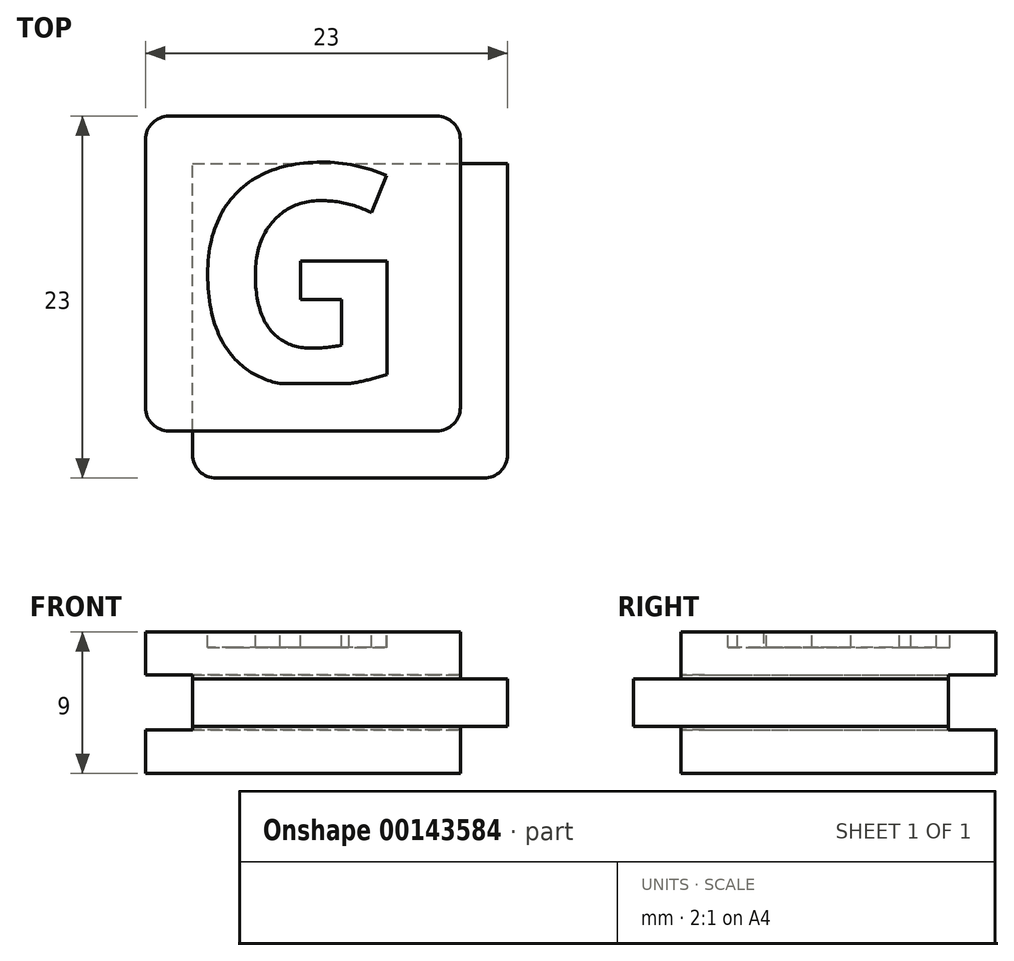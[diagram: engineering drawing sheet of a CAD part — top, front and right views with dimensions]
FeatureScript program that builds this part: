
annotation { "Feature Type Name" : "Feature", "Feature Type Description" : "" }
export const myFeature = defineFeature(function(context is Context, id is Id, definition is map)
    precondition{}
    {
        {
            var Q0;
            Q0=qCreatedBy(makeId("Front.planeOp"),FACE);
            var sketch = newSketch(context, id + "F0", { "sketchPlane" : qUnion([Q0])});
            skLineSegment(sketch, "E0.bottom", {"start": v(10, 4.5) * mm, "end": v(-10, 4.5) * mm});
            skLineSegment(sketch, "E0.top", {"start": v(10, -4.5) * mm, "end": v(-10, -4.5) * mm});
            skLineSegment(sketch, "E0.left", {"start": v(10, 4.5) * mm, "end": v(10, -4.5) * mm});
            skLineSegment(sketch, "E0.right", {"start": v(-10, 4.5) * mm, "end": v(-10, -4.5) * mm});
            skPoint(sketch, "E0.middle", {"position": v(0, 0) * mm});
            skLineSegment(sketch, "E1.bottom", {"start": v(13, 1.5) * mm, "end": v(7, 1.5) * mm});
            skLineSegment(sketch, "E1.top", {"start": v(13, -1.5) * mm, "end": v(7, -1.5) * mm});
            skLineSegment(sketch, "E1.left", {"start": v(13, 1.5) * mm, "end": v(13, -1.5) * mm});
            skLineSegment(sketch, "E1.right", {"start": v(7, 1.5) * mm, "end": v(7, -1.5) * mm});
            skPoint(sketch, "E1.middle", {"position": v(10, 0) * mm});
            skLineSegment(sketch, "E2.bottom", {"start": v(7, 1.5) * mm, "end": v(-7, 1.5) * mm});
            skLineSegment(sketch, "E2.top", {"start": v(7, -1.5) * mm, "end": v(-7, -1.5) * mm});
            skLineSegment(sketch, "E2.right", {"start": v(-7, 1.5) * mm, "end": v(-7, -1.5) * mm});
            skLineSegment(sketch, "E3.bottom", {"start": v(-7, -1.5) * mm, "end": v(-10, -1.5) * mm});
            skLineSegment(sketch, "E3.top", {"start": v(-7, 1.5) * mm, "end": v(-10, 1.5) * mm});
            skLineSegment(sketch, "E3.left", {"start": v(-7, -1.5) * mm, "end": v(-7, 1.5) * mm});
            skLineSegment(sketch, "E3.right", {"start": v(-10, -1.5) * mm, "end": v(-10, 1.5) * mm});
            skSolve(sketch);
        }
        {
            var Q0;
            {var subQ5=sQuery(id+"F0.wireOp",EDGE,"E0.bottom");Q0=makeQuery(id+"F0.imprint","IMPRINT",FACE,{"disambiguationData":[TD([[makeQuery(id+"F0.imprint","IMPRINT",EDGE,{"derivedFrom":subQ5}),1.0]])]});}
            var Q1;
            Q1=makeQuery(id+"F0.imprint","IMPRINT",FACE,{"disambiguationData":[TD([[makeQuery(id+"F0.imprint","IMPRINT",EDGE,{"derivedFrom":sQuery(id+"F0.wireOp",EDGE,"E2.bottom")}),1.0]])]});
            var Q2;
            {var subQ5=sQuery(id+"F0.wireOp",EDGE,"E1.left");Q2=makeQuery(id+"F0.imprint","IMPRINT",FACE,{"disambiguationData":[TD([[makeQuery(id+"F0.imprint","IMPRINT",EDGE,{"derivedFrom":subQ5}),-1.0]])]});}
            var Q3;
            {var subQ5=sQuery(id+"F0.wireOp",EDGE,"E1.right");Q3=makeQuery(id+"F0.imprint","IMPRINT",FACE,{"disambiguationData":[TD([[makeQuery(id+"F0.imprint","IMPRINT",EDGE,{"derivedFrom":subQ5}),1.0]])]});}
            var Q4;
            Q4=makeQuery(id+"F0.imprint","IMPRINT",FACE,{"disambiguationData":[TD([[makeQuery(id+"F0.imprint","IMPRINT",EDGE,{"derivedFrom":sQuery(id+"F0.wireOp",EDGE,"E3.bottom")}),-1.0]])]});
            var Q5;
            {var subQ5=sQuery(id+"F0.wireOp",EDGE,"E0.top");Q5=makeQuery(id+"F0.imprint","IMPRINT",FACE,{"disambiguationData":[TD([[makeQuery(id+"F0.imprint","IMPRINT",EDGE,{"derivedFrom":subQ5}),-1.0]])]});}
            extrude(context, id + "F1", {"entities" : qUnion([Q0, Q1, Q2, Q3, Q4, Q5]), "oppositeDirection" : true, "depth" : 20 * mm});
        }
        {
            var Q0;
            Q0=makeQuery(id+"F0.imprint","IMPRINT",FACE,{"disambiguationData":[TD([[makeQuery(id+"F0.imprint","IMPRINT",EDGE,{"derivedFrom":sQuery(id+"F0.wireOp",EDGE,"E3.bottom")}),-1.0]])]});
            var Q1;
            Q1=makeQuery(id+"F0.imprint","IMPRINT",FACE,{"disambiguationData":[TD([[makeQuery(id+"F0.imprint","IMPRINT",EDGE,{"derivedFrom":sQuery(id+"F0.wireOp",EDGE,"E2.bottom")}),1.0]])]});
            var Q2;
            {var subQ5=sQuery(id+"F0.wireOp",EDGE,"E1.right");Q2=makeQuery(id+"F0.imprint","IMPRINT",FACE,{"disambiguationData":[TD([[makeQuery(id+"F0.imprint","IMPRINT",EDGE,{"derivedFrom":subQ5}),1.0]])]});}
            var Q3;
            {var subQ5=sQuery(id+"F0.wireOp",EDGE,"E1.left");Q3=makeQuery(id+"F0.imprint","IMPRINT",FACE,{"disambiguationData":[TD([[makeQuery(id+"F0.imprint","IMPRINT",EDGE,{"derivedFrom":subQ5}),-1.0]])]});}
            extrude(context, id + "F2", {"entities" : qUnion([Q0, Q1, Q2, Q3]), "operationType" : NewBodyOperationType.ADD, "depth" : 3 * mm});
        }
        {
            var Q0;
            {var subQ0=sQuery(id+"F0.wireOp",EDGE,"E1.left");Q0=makeQuery(id+"F2.boolean.opBoolean","MERGE",FACE,{"derivedFrom":[makeQuery(id+"F1.opExtrude","SWEPT_FACE",FACE,{"disambiguationData":[OSD([subQ0])]}),makeQuery(id+"F2.opExtrude","SWEPT_FACE",FACE,{"disambiguationData":[OSD([subQ0])]})]});}
            var sketch = newSketch(context, id + "F3", { "sketchPlane" : qUnion([Q0])});
            skLineSegment(sketch, "E4.bottom", {"start": v(23, 1.75) * mm, "end": v(17, 1.75) * mm});
            skLineSegment(sketch, "E4.top", {"start": v(23, -1.75) * mm, "end": v(17, -1.75) * mm});
            skLineSegment(sketch, "E4.left", {"start": v(23, 1.75) * mm, "end": v(23, -1.75) * mm});
            skLineSegment(sketch, "E4.right", {"start": v(17, 1.75) * mm, "end": v(17, -1.75) * mm});
            skPoint(sketch, "E4.middle", {"position": v(20, 0) * mm});
            skSolve(sketch);
        }
        {
            var Q0;
            {var subQ1=sQuery(id+"F3.wireOp",EDGE,"E4.bottom");Q0=makeQuery(id+"F3.imprint","IMPRINT",FACE,{"disambiguationData":[TD([[makeQuery(id+"F3.imprint","IMPRINT",EDGE,{"derivedFrom":subQ1}),1.0]])]});}
            var Q1;
            {var subQ1=sQuery(id+"F0.wireOp",EDGE,"E1.left");var subQ8=makeQuery(id+"F1.opExtrude","CAP_EDGE",EDGE,{"disambiguationData":[OSD([subQ1])],"isStart":false});Q1=makeQuery(id+"F3.imprint","IMPRINT",FACE,{"disambiguationData":[TD([[makeQuery(id+"F3.imprint","IMPRINT",EDGE,{"derivedFrom":subQ8}),-1.0]])]});}
            extrude(context, id + "F4", {"entities" : qUnion([Q0, Q1]), "operationType" : NewBodyOperationType.REMOVE, "oppositeDirection" : true, "depth" : 100 * mm});
        }
        {
            var Q0;
            Q0=makeQuery(id+"F4.boolean.opBoolean","COPY",FACE,{"derivedFrom":makeQuery(id+"F4.opExtrude","SWEPT_FACE",FACE,{"disambiguationData":[OSD([sQuery(id+"F3.wireOp",EDGE,"E4.right")])]})});
            var sketch = newSketch(context, id + "F5", { "sketchPlane" : qUnion([Q0])});
            skLineSegment(sketch, "E5.bottom", {"start": v(13, 1.75) * mm, "end": v(7, 1.75) * mm});
            skLineSegment(sketch, "E5.top", {"start": v(13, -1.75) * mm, "end": v(7, -1.75) * mm});
            skLineSegment(sketch, "E5.left", {"start": v(13, 1.75) * mm, "end": v(13, -1.75) * mm});
            skLineSegment(sketch, "E5.right", {"start": v(7, 1.75) * mm, "end": v(7, -1.75) * mm});
            skPoint(sketch, "E5.middle", {"position": v(10, 0) * mm});
            skSolve(sketch);
        }
        {
            var Q0;
            {var subQ3=sQuery(id+"F5.wireOp",EDGE,"E5.left");Q0=makeQuery(id+"F5.imprint","IMPRINT",FACE,{"disambiguationData":[TD([[makeQuery(id+"F5.imprint","IMPRINT",EDGE,{"derivedFrom":subQ3}),-1.0]])]});}
            var Q1;
            {var subQ4=sQuery(id+"F5.wireOp",EDGE,"E5.right");Q1=makeQuery(id+"F5.imprint","IMPRINT",FACE,{"disambiguationData":[TD([[makeQuery(id+"F5.imprint","IMPRINT",EDGE,{"derivedFrom":subQ4}),1.0]])]});}
            extrude(context, id + "F6", {"entities" : qUnion([Q0, Q1]), "operationType" : NewBodyOperationType.REMOVE, "oppositeDirection" : true, "depth" : 100 * mm});
        }
        {
            var Q0;
            Q0=makeQuery(id+"F6.boolean.opBoolean","INTERSECT",EDGE,{"derivedFrom":[makeQuery(id+"F2.opExtrude","CAP_FACE",FACE,{"disambiguationData":[OSD([sQuery(id+"F0.wireOp",EDGE,"E1.bottom"),sQuery(id+"F0.wireOp",EDGE,"E1.top"),sQuery(id+"F0.wireOp",EDGE,"E1.left"),sQuery(id+"F0.wireOp",EDGE,"E2.bottom"),sQuery(id+"F0.wireOp",EDGE,"E2.top"),sQuery(id+"F0.wireOp",EDGE,"E3.bottom"),sQuery(id+"F0.wireOp",EDGE,"E3.top"),sQuery(id+"F0.wireOp",EDGE,"E3.right")])],"isStart":false}),makeQuery(id+"F6.opExtrude","SWEPT_FACE",FACE,{"disambiguationData":[OSD([sQuery(id+"F5.wireOp",EDGE,"E5.right")])]})]});
            var Q1;
            Q1=makeQuery(id+"F2.opExtrude","CAP_EDGE",EDGE,{"disambiguationData":[OSD([sQuery(id+"F0.wireOp",EDGE,"E1.left")])],"isStart":false});
            var Q2;
            {var subQ0=sQuery(id+"F0.wireOp",EDGE,"E0.left");Q2=makeQuery(id+"F1.opExtrude","CAP_EDGE",EDGE,{"disambiguationData":[OSD([subQ0]),TDD([makeQuery(id+"F0.imprint","IMPRINT",EDGE,{"disambiguationData":[TD([[makeQuery(id+"F0.imprint","INTERSECT",VERTEX,{"derivedFrom":[sQuery(id+"F0.wireOp",EDGE,"E0.bottom"),subQ0]}),-1.0]])],"derivedFrom":subQ0})])],"isStart":true});}
            var Q3;
            {var subQ0=sQuery(id+"F0.wireOp",EDGE,"E0.left");Q3=makeQuery(id+"F1.opExtrude","CAP_EDGE",EDGE,{"disambiguationData":[OSD([subQ0]),TDD([makeQuery(id+"F0.imprint","IMPRINT",EDGE,{"disambiguationData":[TD([[makeQuery(id+"F0.imprint","INTERSECT",VERTEX,{"derivedFrom":[sQuery(id+"F0.wireOp",EDGE,"E0.top"),subQ0]}),1.0]])],"derivedFrom":subQ0})])],"isStart":true});}
            var Q4;
            {var subQ0=sQuery(id+"F0.wireOp",EDGE,"E3.right");var subQ1=sQuery(id+"F0.wireOp",EDGE,"E0.right");var subQ3=sQuery(id+"F0.wireOp",EDGE,"E0.top");Q4=makeQuery(id+"F2.boolean.opBoolean","SPLIT",EDGE,{"disambiguationData":[TD([makeQuery(id+"F1.opExtrude","SWEPT_FACE",FACE,{"disambiguationData":[OSD([subQ3])]})])],"derivedFrom":makeQuery(id+"F1.opExtrude","CAP_EDGE",EDGE,{"disambiguationData":[OSD([subQ1,subQ0])],"isStart":true})});}
            var Q5;
            {var subQ1=sQuery(id+"F0.wireOp",EDGE,"E3.right");var subQ2=sQuery(id+"F0.wireOp",EDGE,"E0.right");var subQ3=sQuery(id+"F0.wireOp",EDGE,"E0.bottom");Q5=makeQuery(id+"F2.boolean.opBoolean","SPLIT",EDGE,{"disambiguationData":[TD([makeQuery(id+"F1.opExtrude","SWEPT_FACE",FACE,{"disambiguationData":[OSD([subQ3])]})])],"derivedFrom":makeQuery(id+"F1.opExtrude","CAP_EDGE",EDGE,{"disambiguationData":[OSD([subQ2,subQ1])],"isStart":true})});}
            var Q6;
            Q6=makeQuery(id+"F6.boolean.opBoolean","COPY",EDGE,{"derivedFrom":makeQuery(id+"F6.opExtrude","CAP_EDGE",EDGE,{"disambiguationData":[OSD([sQuery(id+"F5.wireOp",EDGE,"E5.right")])],"isStart":true})});
            var Q7;
            {var subQ0=sQuery(id+"F0.wireOp",EDGE,"E3.right");var subQ1=sQuery(id+"F0.wireOp",EDGE,"E0.right");var subQ2=sQuery(id+"F0.wireOp",EDGE,"E0.bottom");Q7=makeQuery(id+"F4.boolean.opBoolean","SPLIT",EDGE,{"disambiguationData":[TD([makeQuery(id+"F1.opExtrude","SWEPT_FACE",FACE,{"disambiguationData":[OSD([subQ2])]})])],"derivedFrom":makeQuery(id+"F1.opExtrude","CAP_EDGE",EDGE,{"disambiguationData":[OSD([subQ1,subQ0])],"isStart":false})});}
            var Q8;
            {var subQ0=sQuery(id+"F0.wireOp",EDGE,"E3.right");var subQ1=sQuery(id+"F0.wireOp",EDGE,"E0.right");var subQ2=sQuery(id+"F0.wireOp",EDGE,"E0.top");Q8=makeQuery(id+"F4.boolean.opBoolean","SPLIT",EDGE,{"disambiguationData":[TD([makeQuery(id+"F1.opExtrude","SWEPT_FACE",FACE,{"disambiguationData":[OSD([subQ2])]})])],"derivedFrom":makeQuery(id+"F1.opExtrude","CAP_EDGE",EDGE,{"disambiguationData":[OSD([subQ1,subQ0])],"isStart":false})});}
            var Q9;
            Q9=makeQuery(id+"F4.boolean.opBoolean","COPY",EDGE,{"derivedFrom":makeQuery(id+"F4.opExtrude","CAP_EDGE",EDGE,{"disambiguationData":[OSD([sQuery(id+"F3.wireOp",EDGE,"E4.right")])],"isStart":true})});
            var Q10;
            {var subQ0=sQuery(id+"F0.wireOp",EDGE,"E0.left");Q10=makeQuery(id+"F1.opExtrude","CAP_EDGE",EDGE,{"disambiguationData":[OSD([subQ0]),TDD([makeQuery(id+"F0.imprint","IMPRINT",EDGE,{"disambiguationData":[TD([[makeQuery(id+"F0.imprint","INTERSECT",VERTEX,{"derivedFrom":[sQuery(id+"F0.wireOp",EDGE,"E0.bottom"),subQ0]}),-1.0]])],"derivedFrom":subQ0})])],"isStart":false});}
            var Q11;
            {var subQ0=sQuery(id+"F0.wireOp",EDGE,"E0.left");Q11=makeQuery(id+"F1.opExtrude","CAP_EDGE",EDGE,{"disambiguationData":[OSD([subQ0]),TDD([makeQuery(id+"F0.imprint","IMPRINT",EDGE,{"disambiguationData":[TD([[makeQuery(id+"F0.imprint","INTERSECT",VERTEX,{"derivedFrom":[sQuery(id+"F0.wireOp",EDGE,"E0.top"),subQ0]}),1.0]])],"derivedFrom":subQ0})])],"isStart":false});}
            fillet(context, id + "F7", {"entities" : qUnion([Q0, Q1, Q2, Q3, Q4, Q5, Q6, Q7, Q8, Q9, Q10, Q11]), "radius" : 1.5 * mm, "tangentPropagation" : true, "allowEdgeOverflow" : false});
        }
        {
            var Q0;
            Q0=makeQuery(id+"F1.opExtrude","SWEPT_FACE",FACE,{"disambiguationData":[OSD([sQuery(id+"F0.wireOp",EDGE,"E0.bottom")])]});
            var sketch = newSketch(context, id + "F8", { "sketchPlane" : qUnion([Q0])});
            skText(sketch, "E6", { "text": "G", "fontName": "OpenSans-Bold.ttf"});
            skLineSegment(sketch, "E7.0", {"start": v(10.5, 3) * mm, "end": v(-11.07, 3) * mm});
            const initialGuessF8  = {"E6": [-0.00718, 0.003, 1, 0, 0.014]};
            skSetInitialGuess(sketch, initialGuessF8);
            skSolve(sketch);
        }
        {
            var Q0;
            {var subQ0=sQuery(id+"F8.wireOp",EDGE,"E6.sketch_text.stroke-1");Q0=makeQuery(id+"F8.imprint","IMPRINT",FACE,{"disambiguationData":[TD([[makeQuery(id+"F8.imprint","IMPRINT",EDGE,{"derivedFrom":subQ0}),-1.0]])]});}
            extrude(context, id + "F9", {"entities" : qUnion([Q0]), "operationType" : NewBodyOperationType.REMOVE, "oppositeDirection" : true, "depth" : 1 * mm});
        }
    });
